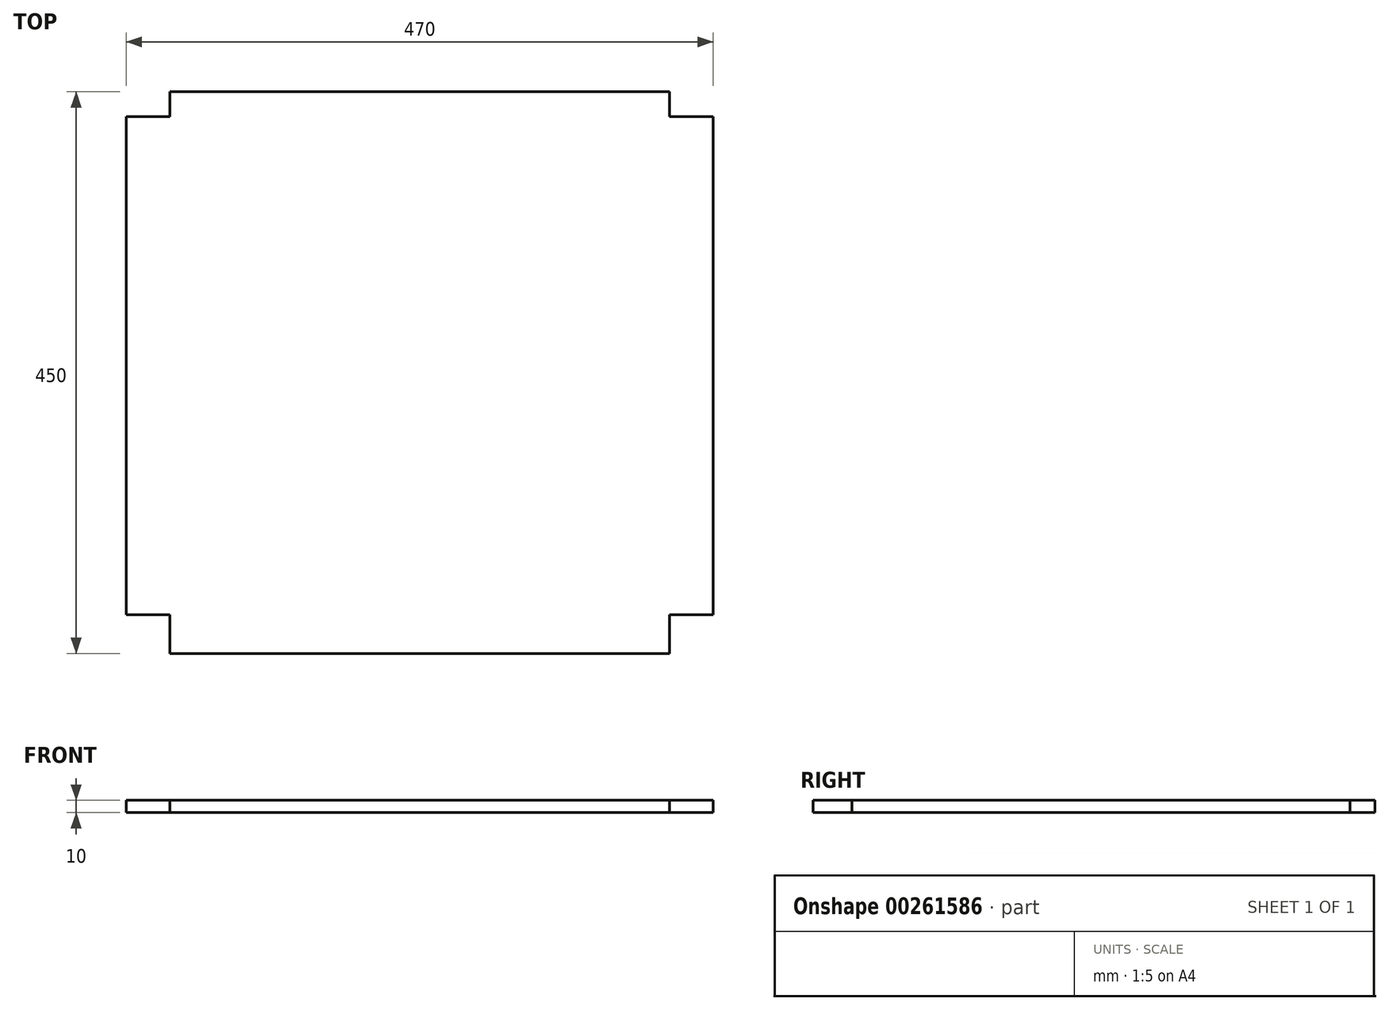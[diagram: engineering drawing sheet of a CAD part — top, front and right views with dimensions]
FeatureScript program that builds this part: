
annotation { "Feature Type Name" : "Feature", "Feature Type Description" : "" }
export const myFeature = defineFeature(function(context is Context, id is Id, definition is map)
    precondition{}
    {
        {
            var Q0;
            Q0=qCreatedBy(makeId("Top.planeOp"),FACE);
            var sketch = newSketch(context, id + "F0", { "sketchPlane" : qUnion([Q0])});
            skLineSegment(sketch, "E0", {"start": v(0, 0) * mm, "end": v(470, 0) * mm});
            skLineSegment(sketch, "E1", {"start": v(470, 0) * mm, "end": v(470, 450) * mm});
            skLineSegment(sketch, "E2", {"start": v(470, 450) * mm, "end": v(0, 450) * mm});
            skLineSegment(sketch, "E3", {"start": v(0, 450) * mm, "end": v(0, 0) * mm});
            skSolve(sketch);
        }
        {
            var Q0;
            Q0 = qSketchRegion(id + "F0", true);
            extrude(context, id + "F1", {"entities" : qUnion([Q0]), "depth" : 10 * mm});
        }
        {
            var Q0;
            Q0=makeQuery(id+"F1.opExtrude","CAP_FACE",FACE,{"disambiguationData":[OSD([sQuery(id+"F0.wireOp",EDGE,"E0"),sQuery(id+"F0.wireOp",EDGE,"E1"),sQuery(id+"F0.wireOp",EDGE,"E2"),sQuery(id+"F0.wireOp",EDGE,"E3")])],"isStart":false});
            var sketch = newSketch(context, id + "F2", { "sketchPlane" : qUnion([Q0])});
            skLineSegment(sketch, "E4.bottom", {"start": v(35, 450) * mm, "end": v(0, 450) * mm});
            skLineSegment(sketch, "E4.top", {"start": v(35, 430) * mm, "end": v(0, 430) * mm});
            skLineSegment(sketch, "E4.left", {"start": v(35, 450) * mm, "end": v(35, 430) * mm});
            skLineSegment(sketch, "E4.right", {"start": v(0, 450) * mm, "end": v(0, 430) * mm});
            skLineSegment(sketch, "E5.bottom", {"start": v(0, 0) * mm, "end": v(35, 0) * mm});
            skLineSegment(sketch, "E5.top", {"start": v(0, 31) * mm, "end": v(35, 31) * mm});
            skLineSegment(sketch, "E5.left", {"start": v(0, 0) * mm, "end": v(0, 31) * mm});
            skLineSegment(sketch, "E5.right", {"start": v(35, 0) * mm, "end": v(35, 31) * mm});
            skLineSegment(sketch, "E6", {"start": v(235, 450) * mm, "end": v(235, 0) * mm, "construction": true});
            skLineSegment(sketch, "E7.MirrorCS", {"start": v(470, 450) * mm, "end": v(470, 430) * mm});
            skLineSegment(sketch, "E8.MirrorCS", {"start": v(435, 450) * mm, "end": v(470, 450) * mm});
            skLineSegment(sketch, "E9.MirrorCS", {"start": v(435, 430) * mm, "end": v(470, 430) * mm});
            skLineSegment(sketch, "E10.MirrorCS", {"start": v(435, 450) * mm, "end": v(435, 430) * mm});
            skLineSegment(sketch, "E11.MirrorCS", {"start": v(470, 31) * mm, "end": v(435, 31) * mm});
            skLineSegment(sketch, "E12.MirrorCS", {"start": v(470, 0) * mm, "end": v(435, 0) * mm});
            skLineSegment(sketch, "E13.MirrorCS", {"start": v(435, 0) * mm, "end": v(435, 31) * mm});
            skLineSegment(sketch, "E14.MirrorCS", {"start": v(470, 0) * mm, "end": v(470, 31) * mm});
            skSolve(sketch);
        }
        {
            var Q0;
            Q0 = qSketchRegion(id + "F2", true);
            extrude(context, id + "F3", {"entities" : qUnion([Q0]), "operationType" : NewBodyOperationType.REMOVE, "endBound" : BoundingType.THROUGH_ALL, "oppositeDirection" : true, "depth" : 25 * mm});
        }
    });
